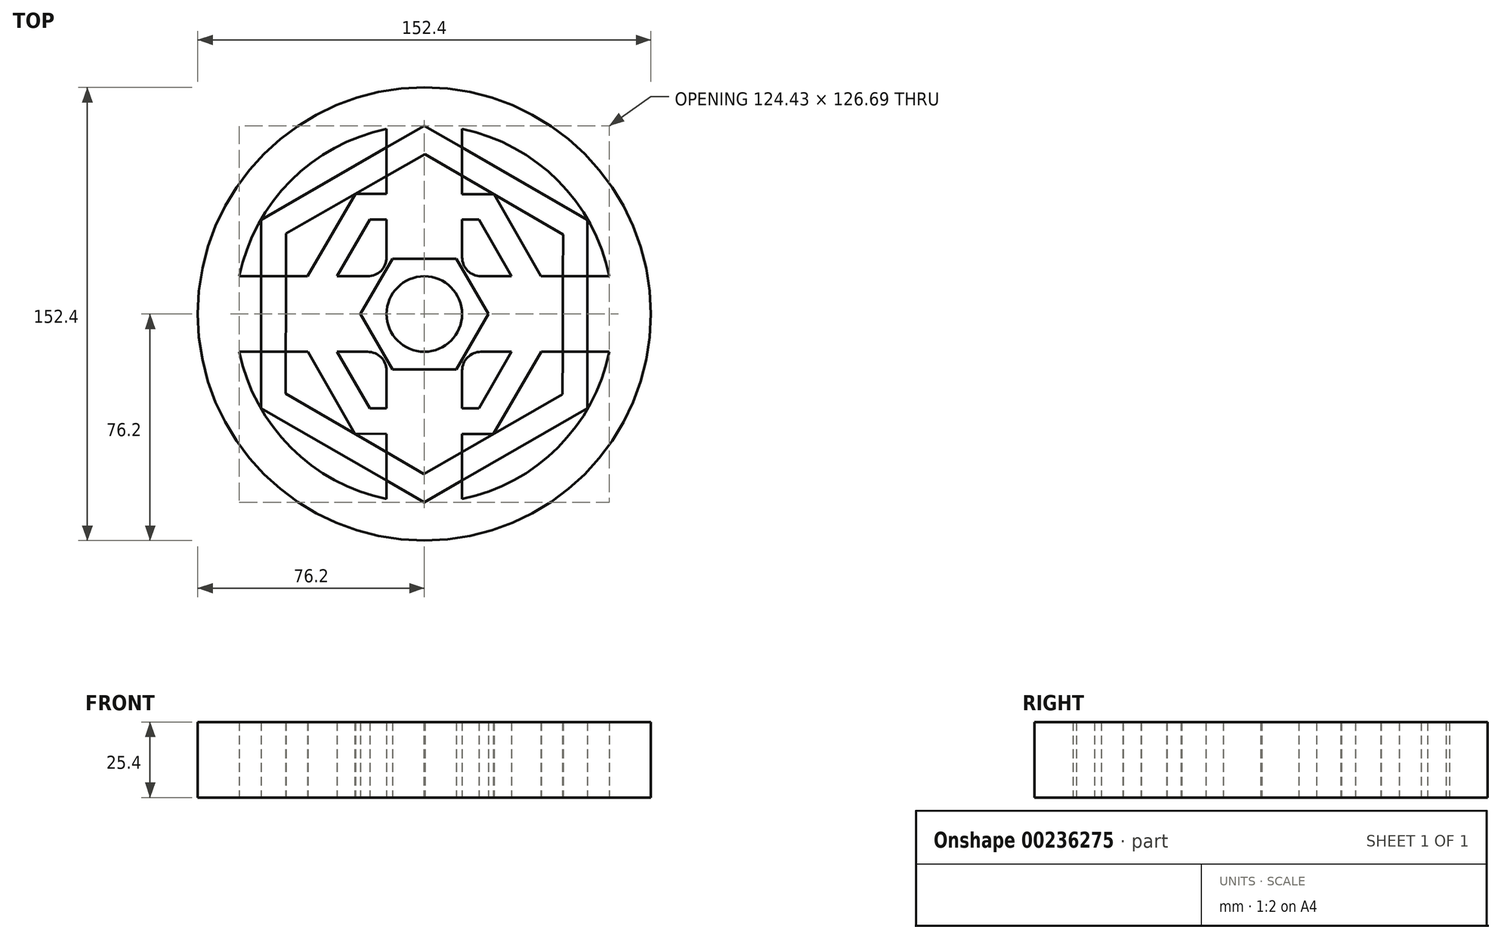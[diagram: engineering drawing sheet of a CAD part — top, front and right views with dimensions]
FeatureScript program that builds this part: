
annotation { "Feature Type Name" : "Feature", "Feature Type Description" : "" }
export const myFeature = defineFeature(function(context is Context, id is Id, definition is map)
    precondition{}
    {
        {
            var Q0;
            Q0=qCreatedBy(makeId("Top.planeOp"),FACE);
            var sketch = newSketch(context, id + "F0", { "sketchPlane" : qUnion([Q0])});
            skCircle(sketch, "E0", {"center": v(0, 0) * mm, "radius": 76.2 * mm});
            skArc(sketch, "E1", {"start": v(62.22, 12.7) * mm, "mid": v(44.9, 44.9) * mm, "end": v(12.7, 62.22) * mm});
            skCircle(sketch, "E2", {"center": v(0, 0) * mm, "radius": 12.7 * mm});
            skLineSegment(sketch, "E3", {"start": v(0, 0) * mm, "end": v(0, 63.5) * mm});
            skLineSegment(sketch, "E4.0", {"start": v(12.7, 19.05) * mm, "end": v(12.7, 62.22) * mm});
            skLineSegment(sketch, "E5.0", {"start": v(-12.7, 19.05) * mm, "end": v(-12.7, 62.22) * mm});
            skLineSegment(sketch, "E6", {"start": v(0, 0) * mm, "end": v(63.5, 0) * mm});
            skLineSegment(sketch, "E7", {"start": v(0, 0) * mm, "end": v(0, -63.5) * mm});
            skLineSegment(sketch, "E8", {"start": v(0, 0) * mm, "end": v(-63.5, 0) * mm});
            skLineSegment(sketch, "E9.0", {"start": v(-19.05, -12.7) * mm, "end": v(-62.22, -12.7) * mm});
            skLineSegment(sketch, "E10.0", {"start": v(-19.05, 12.7) * mm, "end": v(-62.22, 12.7) * mm});
            skLineSegment(sketch, "E11.0", {"start": v(19.05, -12.7) * mm, "end": v(62.22, -12.7) * mm});
            skLineSegment(sketch, "E12.0", {"start": v(19.05, 12.7) * mm, "end": v(62.22, 12.7) * mm});
            skLineSegment(sketch, "E13.0", {"start": v(-12.7, -19.05) * mm, "end": v(-12.7, -62.22) * mm});
            skLineSegment(sketch, "E14.0", {"start": v(12.7, -19.05) * mm, "end": v(12.7, -62.22) * mm});
            skLineSegment(sketch, "E15.trimOffspring", {"start": v(-75.13, 12.7) * mm, "end": v(-76.2, 12.7) * mm});
            skLineSegment(sketch, "E16.trimOffspring", {"start": v(-75.13, -12.7) * mm, "end": v(-76.2, -12.7) * mm});
            skLineSegment(sketch, "E17.trimOffspring", {"start": v(-12.7, -75.13) * mm, "end": v(-12.7, -76.2) * mm});
            skLineSegment(sketch, "E18.trimOffspring", {"start": v(12.7, -75.13) * mm, "end": v(12.7, -76.2) * mm});
            skLineSegment(sketch, "E19.trimOffspring", {"start": v(75.13, -12.7) * mm, "end": v(76.2, -12.7) * mm});
            skLineSegment(sketch, "E20.trimOffspring", {"start": v(75.13, 12.7) * mm, "end": v(76.2, 12.7) * mm});
            skLineSegment(sketch, "E21.trimOffspring", {"start": v(-12.7, 75.13) * mm, "end": v(-12.7, 76.2) * mm});
            skLineSegment(sketch, "E22.trimOffspring", {"start": v(12.7, 75.13) * mm, "end": v(12.7, 76.2) * mm});
            skArc(sketch, "E23.trimOffspring", {"start": v(12.7, -62.22) * mm, "mid": v(44.9, -44.9) * mm, "end": v(62.22, -12.7) * mm});
            skArc(sketch, "E24.trimOffspring", {"start": v(-62.22, -12.7) * mm, "mid": v(-44.9, -44.9) * mm, "end": v(-12.7, -62.22) * mm});
            skArc(sketch, "E25.trimOffspring", {"start": v(-12.7, 62.22) * mm, "mid": v(-44.9, 44.9) * mm, "end": v(-62.22, 12.7) * mm});
            skPoint(sketch, "E26.visualSharp", {"position": v(-12.7, 12.7) * mm});
            skArc(sketch, "E26.filletArc", {"start": v(-19.05, 12.7) * mm, "mid": v(-14.56, 14.56) * mm, "end": v(-12.7, 19.05) * mm});
            skPoint(sketch, "E27.visualSharp", {"position": v(12.7, 12.7) * mm});
            skArc(sketch, "E27.filletArc", {"start": v(12.7, 19.05) * mm, "mid": v(14.56, 14.56) * mm, "end": v(19.05, 12.7) * mm});
            skPoint(sketch, "E28.visualSharp", {"position": v(12.7, -12.7) * mm});
            skArc(sketch, "E28.filletArc", {"start": v(19.05, -12.7) * mm, "mid": v(14.56, -14.56) * mm, "end": v(12.7, -19.05) * mm});
            skPoint(sketch, "E29.visualSharp", {"position": v(-12.7, -12.7) * mm});
            skArc(sketch, "E29.filletArc", {"start": v(-12.7, -19.05) * mm, "mid": v(-14.56, -14.56) * mm, "end": v(-19.05, -12.7) * mm});
            skCircle(sketch, "E30.cCircle", {"center": v(0, 0) * mm, "radius": 40.32 * mm, "construction": true});
            skLineSegment(sketch, "E30.0", {"start": v(23.4, 40.25) * mm, "end": v(46.56, -0.14) * mm});
            skLineSegment(sketch, "E30.1", {"start": v(46.56, -0.14) * mm, "end": v(23.16, -40.4) * mm});
            skLineSegment(sketch, "E30.2", {"start": v(23.16, -40.4) * mm, "end": v(-23.4, -40.25) * mm});
            skLineSegment(sketch, "E30.3", {"start": v(-23.4, -40.25) * mm, "end": v(-46.56, 0.14) * mm});
            skLineSegment(sketch, "E30.4", {"start": v(-46.56, 0.14) * mm, "end": v(-23.16, 40.4) * mm});
            skLineSegment(sketch, "E30.5", {"start": v(-23.16, 40.4) * mm, "end": v(23.4, 40.25) * mm});
            skPoint(sketch, "E30.0.midPoint", {"position": v(34.98, 20.05) * mm});
            skCircle(sketch, "E31.cCircle", {"center": v(0, 0) * mm, "radius": 31.75 * mm, "construction": true});
            skLineSegment(sketch, "E31.0", {"start": v(18.33, -31.75) * mm, "end": v(-18.33, -31.75) * mm});
            skLineSegment(sketch, "E31.1", {"start": v(-18.33, -31.75) * mm, "end": v(-36.66, 0) * mm});
            skLineSegment(sketch, "E31.2", {"start": v(-36.66, 0) * mm, "end": v(-18.33, 31.75) * mm});
            skLineSegment(sketch, "E31.3", {"start": v(-18.33, 31.75) * mm, "end": v(18.33, 31.75) * mm});
            skLineSegment(sketch, "E31.4", {"start": v(18.33, 31.75) * mm, "end": v(36.66, 0) * mm});
            skLineSegment(sketch, "E31.5", {"start": v(36.66, 0) * mm, "end": v(18.33, -31.75) * mm});
            skPoint(sketch, "E31.0.midPoint", {"position": v(0, -31.75) * mm});
            skCircle(sketch, "E32.cCircle", {"center": v(0, 0) * mm, "radius": 54.86 * mm, "construction": true});
            skLineSegment(sketch, "E32.0", {"start": v(0, 63.35) * mm, "end": v(54.86, 31.67) * mm});
            skLineSegment(sketch, "E32.1", {"start": v(54.86, 31.67) * mm, "end": v(54.86, -31.67) * mm});
            skLineSegment(sketch, "E32.2", {"start": v(54.86, -31.67) * mm, "end": v(0, -63.35) * mm});
            skLineSegment(sketch, "E32.3", {"start": v(0, -63.35) * mm, "end": v(-54.86, -31.67) * mm});
            skLineSegment(sketch, "E32.4", {"start": v(-54.86, -31.67) * mm, "end": v(-54.86, 31.67) * mm});
            skLineSegment(sketch, "E32.5", {"start": v(-54.86, 31.67) * mm, "end": v(0, 63.35) * mm});
            skPoint(sketch, "E32.0.midPoint", {"position": v(27.43, 47.5) * mm});
            skCircle(sketch, "E33.cCircle", {"center": v(0, 0) * mm, "radius": 46.56 * mm, "construction": true});
            skLineSegment(sketch, "E33.0", {"start": v(0.17, 53.77) * mm, "end": v(46.65, 26.74) * mm});
            skLineSegment(sketch, "E33.1", {"start": v(46.65, 26.74) * mm, "end": v(46.48, -27.03) * mm});
            skLineSegment(sketch, "E33.2", {"start": v(46.48, -27.03) * mm, "end": v(-0.17, -53.77) * mm});
            skLineSegment(sketch, "E33.3", {"start": v(-0.17, -53.77) * mm, "end": v(-46.65, -26.74) * mm});
            skLineSegment(sketch, "E33.4", {"start": v(-46.65, -26.74) * mm, "end": v(-46.48, 27.03) * mm});
            skLineSegment(sketch, "E33.5", {"start": v(-46.48, 27.03) * mm, "end": v(0.17, 53.77) * mm});
            skPoint(sketch, "E33.0.midPoint", {"position": v(23.4, 40.25) * mm});
            skCircle(sketch, "E34.cCircle", {"center": v(0, 0) * mm, "radius": 18.62 * mm, "construction": true});
            skLineSegment(sketch, "E34.0", {"start": v(10.75, 18.61) * mm, "end": v(21.5, 0) * mm});
            skLineSegment(sketch, "E34.1", {"start": v(21.5, 0) * mm, "end": v(10.74, -18.62) * mm});
            skLineSegment(sketch, "E34.2", {"start": v(10.74, -18.62) * mm, "end": v(-10.75, -18.61) * mm});
            skLineSegment(sketch, "E34.3", {"start": v(-10.75, -18.61) * mm, "end": v(-21.5, 0) * mm});
            skLineSegment(sketch, "E34.4", {"start": v(-21.5, 0) * mm, "end": v(-10.74, 18.62) * mm});
            skLineSegment(sketch, "E34.5", {"start": v(-10.74, 18.62) * mm, "end": v(10.75, 18.61) * mm});
            skPoint(sketch, "E34.0.midPoint", {"position": v(16.13, 9.3) * mm});
            skCircle(sketch, "E35.cCircle", {"center": v(0, 0) * mm, "radius": 15 * mm, "construction": true});
            skLineSegment(sketch, "E35.0", {"start": v(8.73, 14.96) * mm, "end": v(17.32, -0.08) * mm});
            skLineSegment(sketch, "E35.1", {"start": v(17.32, -0.08) * mm, "end": v(8.6, -15.04) * mm});
            skLineSegment(sketch, "E35.2", {"start": v(8.6, -15.04) * mm, "end": v(-8.73, -14.96) * mm});
            skLineSegment(sketch, "E35.3", {"start": v(-8.73, -14.96) * mm, "end": v(-17.32, 0.08) * mm});
            skLineSegment(sketch, "E35.4", {"start": v(-17.32, 0.08) * mm, "end": v(-8.6, 15.04) * mm});
            skLineSegment(sketch, "E35.5", {"start": v(-8.6, 15.04) * mm, "end": v(8.73, 14.96) * mm});
            skPoint(sketch, "E35.0.midPoint", {"position": v(13.02, 7.44) * mm});
            skSolve(sketch);
        }
        {
            var Q0;
            Q0 = qSketchRegion(id + "F0", true);
            var Q1;
            {var subQ3=sQuery(id+"F0.wireOp",EDGE,"E5.0");var subQ9=sQuery(id+"F0.wireOp",EDGE,"E31.3");var subQ10=makeQuery(id+"F0.imprint","INTERSECT",VERTEX,{"derivedFrom":[subQ3,subQ9]});Q1=makeQuery(id+"F0.imprint","IMPRINT",FACE,{"disambiguationData":[TD([[makeQuery(id+"F0.imprint","IMPRINT",EDGE,{"disambiguationData":[TD([[subQ10,-1.0]])],"derivedFrom":subQ3}),1.0]])]});}
            var Q2;
            {var subQ3=sQuery(id+"F0.wireOp",EDGE,"E10.0");var subQ7=sQuery(id+"F0.wireOp",EDGE,"E31.2");var subQ8=makeQuery(id+"F0.imprint","INTERSECT",VERTEX,{"derivedFrom":[subQ3,subQ7]});Q2=makeQuery(id+"F0.imprint","IMPRINT",FACE,{"disambiguationData":[TD([[makeQuery(id+"F0.imprint","IMPRINT",EDGE,{"disambiguationData":[TD([[subQ8,-1.0]])],"derivedFrom":subQ3}),1.0]])]});}
            var Q3;
            {var subQ0=sQuery(id+"F0.wireOp",EDGE,"E31.1");var subQ5=sQuery(id+"F0.wireOp",EDGE,"E9.0");var subQ6=makeQuery(id+"F0.imprint","INTERSECT",VERTEX,{"derivedFrom":[subQ5,subQ0]});Q3=makeQuery(id+"F0.imprint","IMPRINT",FACE,{"disambiguationData":[TD([[makeQuery(id+"F0.imprint","IMPRINT",EDGE,{"disambiguationData":[TD([[subQ6,-1.0]])],"derivedFrom":subQ5}),-1.0]])]});}
            var Q4;
            {var subQ3=sQuery(id+"F0.wireOp",EDGE,"E9.0");var subQ9=sQuery(id+"F0.wireOp",EDGE,"E31.1");var subQ10=makeQuery(id+"F0.imprint","INTERSECT",VERTEX,{"derivedFrom":[subQ3,subQ9]});Q4=makeQuery(id+"F0.imprint","IMPRINT",FACE,{"disambiguationData":[TD([[makeQuery(id+"F0.imprint","IMPRINT",EDGE,{"disambiguationData":[TD([[subQ10,-1.0]])],"derivedFrom":subQ3}),1.0]])]});}
            var Q5;
            {var subQ0=sQuery(id+"F0.wireOp",EDGE,"E30.2");var subQ1=sQuery(id+"F0.wireOp",EDGE,"E7");var subQ2=makeQuery(id+"F0.imprint","INTERSECT",VERTEX,{"derivedFrom":[subQ1,subQ0]});Q5=makeQuery(id+"F0.imprint","IMPRINT",FACE,{"disambiguationData":[TD([[makeQuery(id+"F0.imprint","IMPRINT",EDGE,{"disambiguationData":[TD([[subQ2,1.0]])],"derivedFrom":subQ1}),-1.0]])]});}
            var Q6;
            {var subQ0=sQuery(id+"F0.wireOp",EDGE,"E30.2");var subQ1=sQuery(id+"F0.wireOp",EDGE,"E7");var subQ2=makeQuery(id+"F0.imprint","INTERSECT",VERTEX,{"derivedFrom":[subQ1,subQ0]});Q6=makeQuery(id+"F0.imprint","IMPRINT",FACE,{"disambiguationData":[TD([[makeQuery(id+"F0.imprint","IMPRINT",EDGE,{"disambiguationData":[TD([[subQ2,1.0]])],"derivedFrom":subQ1}),1.0]])]});}
            var Q7;
            {var subQ3=sQuery(id+"F0.wireOp",EDGE,"E11.0");var subQ9=sQuery(id+"F0.wireOp",EDGE,"E31.5");var subQ11=makeQuery(id+"F0.imprint","INTERSECT",VERTEX,{"derivedFrom":[subQ3,subQ9]});Q7=makeQuery(id+"F0.imprint","IMPRINT",FACE,{"disambiguationData":[TD([[makeQuery(id+"F0.imprint","IMPRINT",EDGE,{"disambiguationData":[TD([[subQ11,-1.0]])],"derivedFrom":subQ3}),-1.0]])]});}
            var Q8;
            {var subQ3=sQuery(id+"F0.wireOp",EDGE,"E11.0");var subQ7=sQuery(id+"F0.wireOp",EDGE,"E31.5");var subQ8=makeQuery(id+"F0.imprint","INTERSECT",VERTEX,{"derivedFrom":[subQ3,subQ7]});Q8=makeQuery(id+"F0.imprint","IMPRINT",FACE,{"disambiguationData":[TD([[makeQuery(id+"F0.imprint","IMPRINT",EDGE,{"disambiguationData":[TD([[subQ8,-1.0]])],"derivedFrom":subQ3}),1.0]])]});}
            var Q9;
            {var subQ0=sQuery(id+"F0.wireOp",EDGE,"E31.4");var subQ5=sQuery(id+"F0.wireOp",EDGE,"E12.0");var subQ6=makeQuery(id+"F0.imprint","INTERSECT",VERTEX,{"derivedFrom":[subQ5,subQ0]});Q9=makeQuery(id+"F0.imprint","IMPRINT",FACE,{"disambiguationData":[TD([[makeQuery(id+"F0.imprint","IMPRINT",EDGE,{"disambiguationData":[TD([[subQ6,-1.0]])],"derivedFrom":subQ5}),-1.0]])]});}
            var Q10;
            {var subQ3=sQuery(id+"F0.wireOp",EDGE,"E4.0");var subQ9=sQuery(id+"F0.wireOp",EDGE,"E31.3");var subQ11=makeQuery(id+"F0.imprint","INTERSECT",VERTEX,{"derivedFrom":[subQ3,subQ9]});Q10=makeQuery(id+"F0.imprint","IMPRINT",FACE,{"disambiguationData":[TD([[makeQuery(id+"F0.imprint","IMPRINT",EDGE,{"disambiguationData":[TD([[subQ11,-1.0]])],"derivedFrom":subQ3}),-1.0]])]});}
            var Q11;
            {var subQ0=sQuery(id+"F0.wireOp",EDGE,"E30.5");var subQ1=sQuery(id+"F0.wireOp",EDGE,"E3");var subQ2=makeQuery(id+"F0.imprint","INTERSECT",VERTEX,{"derivedFrom":[subQ1,subQ0]});Q11=makeQuery(id+"F0.imprint","IMPRINT",FACE,{"disambiguationData":[TD([[makeQuery(id+"F0.imprint","IMPRINT",EDGE,{"disambiguationData":[TD([[subQ2,1.0]])],"derivedFrom":subQ1}),-1.0]])]});}
            var Q12;
            {var subQ0=sQuery(id+"F0.wireOp",EDGE,"E30.5");var subQ1=sQuery(id+"F0.wireOp",EDGE,"E3");var subQ2=makeQuery(id+"F0.imprint","INTERSECT",VERTEX,{"derivedFrom":[subQ1,subQ0]});Q12=makeQuery(id+"F0.imprint","IMPRINT",FACE,{"disambiguationData":[TD([[makeQuery(id+"F0.imprint","IMPRINT",EDGE,{"disambiguationData":[TD([[subQ2,1.0]])],"derivedFrom":subQ1}),1.0]])]});}
            var Q13;
            {var subQ7=sQuery(id+"F0.wireOp",EDGE,"E27.filletArc");Q13=makeQuery(id+"F0.imprint","IMPRINT",FACE,{"disambiguationData":[TD([[makeQuery(id+"F0.imprint","IMPRINT",EDGE,{"derivedFrom":subQ7}),-1.0]])]});}
            var Q14;
            {var subQ0=sQuery(id+"F0.wireOp",EDGE,"E28.filletArc");Q14=makeQuery(id+"F0.imprint","IMPRINT",FACE,{"disambiguationData":[TD([[makeQuery(id+"F0.imprint","IMPRINT",EDGE,{"derivedFrom":subQ0}),-1.0]])]});}
            var Q15;
            {var subQ0=sQuery(id+"F0.wireOp",EDGE,"E29.filletArc");Q15=makeQuery(id+"F0.imprint","IMPRINT",FACE,{"disambiguationData":[TD([[makeQuery(id+"F0.imprint","IMPRINT",EDGE,{"derivedFrom":subQ0}),-1.0]])]});}
            var Q16;
            {var subQ0=sQuery(id+"F0.wireOp",EDGE,"E26.filletArc");Q16=makeQuery(id+"F0.imprint","IMPRINT",FACE,{"disambiguationData":[TD([[makeQuery(id+"F0.imprint","IMPRINT",EDGE,{"derivedFrom":subQ0}),-1.0]])]});}
            var Q17;
            {var subQ5=sQuery(id+"F0.wireOp",EDGE,"E4.0");var subQ7=sQuery(id+"F0.wireOp",EDGE,"E33.0");var subQ8=makeQuery(id+"F0.imprint","INTERSECT",VERTEX,{"derivedFrom":[subQ5,subQ7]});Q17=makeQuery(id+"F0.imprint","IMPRINT",FACE,{"disambiguationData":[TD([[makeQuery(id+"F0.imprint","IMPRINT",EDGE,{"disambiguationData":[TD([[subQ8,-1.0]])],"derivedFrom":subQ5}),-1.0]])]});}
            var Q18;
            {var subQ7=sQuery(id+"F0.wireOp",EDGE,"E33.1");var subQ9=sQuery(id+"F0.wireOp",EDGE,"E11.0");var subQ12=makeQuery(id+"F0.imprint","INTERSECT",VERTEX,{"derivedFrom":[subQ9,subQ7]});Q18=makeQuery(id+"F0.imprint","IMPRINT",FACE,{"disambiguationData":[TD([[makeQuery(id+"F0.imprint","IMPRINT",EDGE,{"disambiguationData":[TD([[subQ12,-1.0]])],"derivedFrom":subQ9}),-1.0]])]});}
            var Q19;
            {var subQ7=sQuery(id+"F0.wireOp",EDGE,"E9.0");var subQ10=sQuery(id+"F0.wireOp",EDGE,"E33.4");var subQ11=makeQuery(id+"F0.imprint","INTERSECT",VERTEX,{"derivedFrom":[subQ7,subQ10]});Q19=makeQuery(id+"F0.imprint","IMPRINT",FACE,{"disambiguationData":[TD([[makeQuery(id+"F0.imprint","IMPRINT",EDGE,{"disambiguationData":[TD([[subQ11,-1.0]])],"derivedFrom":subQ7}),1.0]])]});}
            var Q20;
            {var subQ3=sQuery(id+"F0.wireOp",EDGE,"E5.0");var subQ9=sQuery(id+"F0.wireOp",EDGE,"E33.5");var subQ10=makeQuery(id+"F0.imprint","INTERSECT",VERTEX,{"derivedFrom":[subQ3,subQ9]});Q20=makeQuery(id+"F0.imprint","IMPRINT",FACE,{"disambiguationData":[TD([[makeQuery(id+"F0.imprint","IMPRINT",EDGE,{"disambiguationData":[TD([[subQ10,-1.0]])],"derivedFrom":subQ3}),1.0]])]});}
            var Q21;
            {var subQ0=sQuery(id+"F0.wireOp",EDGE,"E30.5");var subQ1=sQuery(id+"F0.wireOp",EDGE,"E3");var subQ2=makeQuery(id+"F0.imprint","INTERSECT",VERTEX,{"derivedFrom":[subQ1,subQ0]});Q21=makeQuery(id+"F0.imprint","IMPRINT",FACE,{"disambiguationData":[TD([[makeQuery(id+"F0.imprint","IMPRINT",EDGE,{"disambiguationData":[TD([[subQ2,-1.0]])],"derivedFrom":subQ1}),1.0]])]});}
            var Q22;
            {var subQ0=sQuery(id+"F0.wireOp",EDGE,"E30.5");var subQ1=sQuery(id+"F0.wireOp",EDGE,"E3");var subQ2=makeQuery(id+"F0.imprint","INTERSECT",VERTEX,{"derivedFrom":[subQ1,subQ0]});Q22=makeQuery(id+"F0.imprint","IMPRINT",FACE,{"disambiguationData":[TD([[makeQuery(id+"F0.imprint","IMPRINT",EDGE,{"disambiguationData":[TD([[subQ2,-1.0]])],"derivedFrom":subQ1}),-1.0]])]});}
            var Q23;
            {var subQ0=sQuery(id+"F0.wireOp",EDGE,"E30.0");var subQ1=sQuery(id+"F0.wireOp",EDGE,"E6");var subQ2=makeQuery(id+"F0.imprint","INTERSECT",VERTEX,{"derivedFrom":[subQ1,subQ0]});Q23=makeQuery(id+"F0.imprint","IMPRINT",FACE,{"disambiguationData":[TD([[makeQuery(id+"F0.imprint","IMPRINT",EDGE,{"disambiguationData":[TD([[subQ2,-1.0]])],"derivedFrom":subQ1}),1.0]])]});}
            var Q24;
            {var subQ0=sQuery(id+"F0.wireOp",EDGE,"E30.1");var subQ1=sQuery(id+"F0.wireOp",EDGE,"E11.0");var subQ2=makeQuery(id+"F0.imprint","INTERSECT",VERTEX,{"derivedFrom":[subQ1,subQ0]});Q24=makeQuery(id+"F0.imprint","IMPRINT",FACE,{"disambiguationData":[TD([[makeQuery(id+"F0.imprint","IMPRINT",EDGE,{"disambiguationData":[TD([[subQ2,-1.0]])],"derivedFrom":subQ1}),1.0]])]});}
            var Q25;
            {var subQ0=sQuery(id+"F0.wireOp",EDGE,"E30.2");var subQ1=sQuery(id+"F0.wireOp",EDGE,"E7");var subQ2=makeQuery(id+"F0.imprint","INTERSECT",VERTEX,{"derivedFrom":[subQ1,subQ0]});Q25=makeQuery(id+"F0.imprint","IMPRINT",FACE,{"disambiguationData":[TD([[makeQuery(id+"F0.imprint","IMPRINT",EDGE,{"disambiguationData":[TD([[subQ2,-1.0]])],"derivedFrom":subQ1}),1.0]])]});}
            var Q26;
            {var subQ3=sQuery(id+"F0.wireOp",EDGE,"E7");var subQ5=sQuery(id+"F0.wireOp",EDGE,"E30.2");var subQ9=makeQuery(id+"F0.imprint","INTERSECT",VERTEX,{"derivedFrom":[subQ3,subQ5]});Q26=makeQuery(id+"F0.imprint","IMPRINT",FACE,{"disambiguationData":[TD([[makeQuery(id+"F0.imprint","IMPRINT",EDGE,{"disambiguationData":[TD([[subQ9,-1.0]])],"derivedFrom":subQ3}),-1.0]])]});}
            var Q27;
            {var subQ0=sQuery(id+"F0.wireOp",EDGE,"E30.3");var subQ1=sQuery(id+"F0.wireOp",EDGE,"E8");var subQ2=makeQuery(id+"F0.imprint","INTERSECT",VERTEX,{"derivedFrom":[subQ1,subQ0]});Q27=makeQuery(id+"F0.imprint","IMPRINT",FACE,{"disambiguationData":[TD([[makeQuery(id+"F0.imprint","IMPRINT",EDGE,{"disambiguationData":[TD([[subQ2,-1.0]])],"derivedFrom":subQ1}),1.0]])]});}
            var Q28;
            {var subQ0=sQuery(id+"F0.wireOp",EDGE,"E30.4");var subQ1=sQuery(id+"F0.wireOp",EDGE,"E10.0");var subQ2=makeQuery(id+"F0.imprint","INTERSECT",VERTEX,{"derivedFrom":[subQ1,subQ0]});Q28=makeQuery(id+"F0.imprint","IMPRINT",FACE,{"disambiguationData":[TD([[makeQuery(id+"F0.imprint","IMPRINT",EDGE,{"disambiguationData":[TD([[subQ2,-1.0]])],"derivedFrom":subQ1}),1.0]])]});}
            var Q29;
            {var subQ0=sQuery(id+"F0.wireOp",EDGE,"E3");var subQ1=sQuery(id+"F0.wireOp",EDGE,"E2");var subQ2=makeQuery(id+"F0.imprint","INTERSECT",VERTEX,{"derivedFrom":[subQ1,subQ0]});Q29=makeQuery(id+"F0.imprint","IMPRINT",FACE,{"disambiguationData":[TD([[makeQuery(id+"F0.imprint","IMPRINT",EDGE,{"disambiguationData":[TD([[subQ2,-1.0]])],"derivedFrom":subQ1}),1.0]])]});}
            var Q30;
            {var subQ0=sQuery(id+"F0.wireOp",EDGE,"E3");var subQ1=sQuery(id+"F0.wireOp",EDGE,"E2");var subQ2=makeQuery(id+"F0.imprint","INTERSECT",VERTEX,{"derivedFrom":[subQ1,subQ0]});Q30=makeQuery(id+"F0.imprint","IMPRINT",FACE,{"disambiguationData":[TD([[makeQuery(id+"F0.imprint","IMPRINT",EDGE,{"disambiguationData":[TD([[subQ2,1.0]])],"derivedFrom":subQ1}),1.0]])]});}
            var Q31;
            {var subQ0=sQuery(id+"F0.wireOp",EDGE,"E6");var subQ1=sQuery(id+"F0.wireOp",EDGE,"E2");var subQ2=makeQuery(id+"F0.imprint","INTERSECT",VERTEX,{"derivedFrom":[subQ1,subQ0]});Q31=makeQuery(id+"F0.imprint","IMPRINT",FACE,{"disambiguationData":[TD([[makeQuery(id+"F0.imprint","IMPRINT",EDGE,{"disambiguationData":[TD([[subQ2,1.0]])],"derivedFrom":subQ1}),1.0]])]});}
            var Q32;
            {var subQ0=sQuery(id+"F0.wireOp",EDGE,"E8");var subQ1=sQuery(id+"F0.wireOp",EDGE,"E2");var subQ2=makeQuery(id+"F0.imprint","INTERSECT",VERTEX,{"derivedFrom":[subQ1,subQ0]});Q32=makeQuery(id+"F0.imprint","IMPRINT",FACE,{"disambiguationData":[TD([[makeQuery(id+"F0.imprint","IMPRINT",EDGE,{"disambiguationData":[TD([[subQ2,-1.0]])],"derivedFrom":subQ1}),1.0]])]});}
            extrude(context, id + "F1", {"entities" : qUnion([Q0, Q1, Q2, Q3, Q4, Q5, Q6, Q7, Q8, Q9, Q10, Q11, Q12, Q13, Q14, Q15, Q16, Q17, Q18, Q19, Q20, Q21, Q22, Q23, Q24, Q25, Q26, Q27, Q28, Q29, Q30, Q31, Q32]), "endBound" : BoundingType.SYMMETRIC, "depth" : 25.4 * mm});
        }
    });
